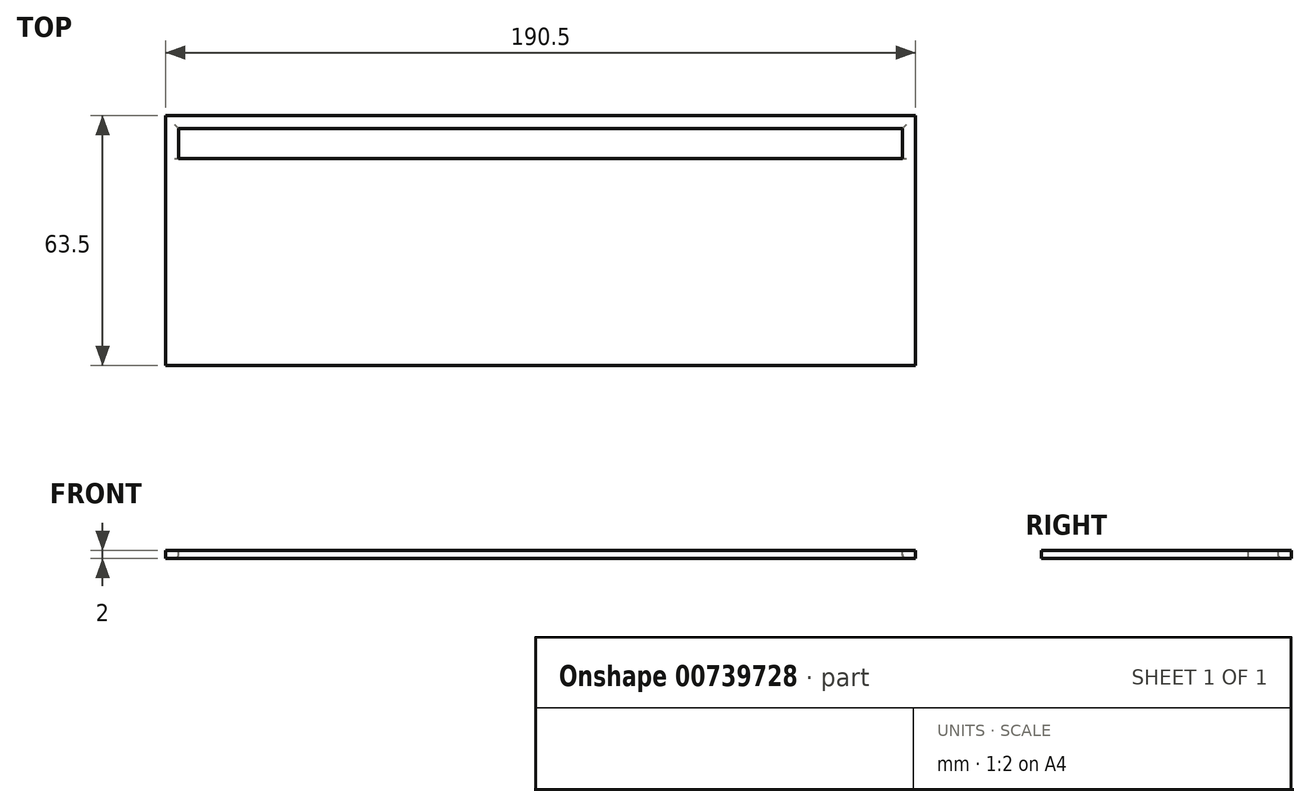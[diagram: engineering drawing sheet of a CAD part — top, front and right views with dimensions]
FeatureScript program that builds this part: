
annotation { "Feature Type Name" : "Feature", "Feature Type Description" : "" }
export const myFeature = defineFeature(function(context is Context, id is Id, definition is map)
    precondition{}
    {
        {
            var Q0;
            Q0=qCreatedBy(makeId("Top.planeOp"),FACE);
            var sketch = newSketch(context, id + "F0", { "sketchPlane" : qUnion([Q0])});
            skLineSegment(sketch, "E0.bottom", {"start": v(-93.46, 63.5) * mm, "end": v(97.04, 63.5) * mm});
            skLineSegment(sketch, "E0.top", {"start": v(-93.46, 0) * mm, "end": v(97.04, 0) * mm});
            skLineSegment(sketch, "E0.left", {"start": v(-93.46, 63.5) * mm, "end": v(-93.46, 0) * mm});
            skLineSegment(sketch, "E0.right", {"start": v(97.04, 63.5) * mm, "end": v(97.04, 0) * mm});
            skSolve(sketch);
        }
        {
            var Q0;
            Q0 = qSketchRegion(id + "F0", true);
            extrude(context, id + "F1", {"entities" : qUnion([Q0]), "depth" : 2 * mm, "offsetDistance" : 25.4 * mm});
        }
        {
            var Q0;
            Q0=makeQuery(id+"F1.opExtrude","CAP_FACE",FACE,{"disambiguationData":[OSD([sQuery(id+"F0.wireOp",EDGE,"E0.bottom"),sQuery(id+"F0.wireOp",EDGE,"E0.top"),sQuery(id+"F0.wireOp",EDGE,"E0.left"),sQuery(id+"F0.wireOp",EDGE,"E0.right")])],"isStart":false});
            var sketch = newSketch(context, id + "F2", { "sketchPlane" : qUnion([Q0])});
            skLineSegment(sketch, "E1.bottom", {"start": v(-90.16, 60.2) * mm, "end": v(93.74, 60.2) * mm});
            skLineSegment(sketch, "E1.top", {"start": v(-90.16, 52.58) * mm, "end": v(93.74, 52.58) * mm});
            skLineSegment(sketch, "E1.left", {"start": v(-90.16, 60.2) * mm, "end": v(-90.16, 52.58) * mm});
            skLineSegment(sketch, "E1.right", {"start": v(93.74, 60.2) * mm, "end": v(93.74, 52.58) * mm});
            skSolve(sketch);
        }
        {
            var Q0;
            Q0 = qSketchRegion(id + "F2", true);
            extrude(context, id + "F3", {"entities" : qUnion([Q0]), "operationType" : NewBodyOperationType.REMOVE, "oppositeDirection" : true, "depth" : 25.4 * mm, "offsetDistance" : 25.4 * mm});
        }
        {
            var Q0;
            Q0=makeQuery(id+"F3.boolean.opBoolean","COPY",EDGE,{"derivedFrom":makeQuery(id+"F3.opExtrude","CAP_EDGE",EDGE,{"disambiguationData":[OSD([sQuery(id+"F2.wireOp",EDGE,"E1.bottom")])],"isStart":true})});
            var Q1;
            Q1=makeQuery(id+"F3.boolean.opBoolean","INTERSECT",EDGE,{"derivedFrom":[makeQuery(id+"F1.opExtrude","CAP_FACE",FACE,{"disambiguationData":[OSD([sQuery(id+"F0.wireOp",EDGE,"E0.bottom"),sQuery(id+"F0.wireOp",EDGE,"E0.top"),sQuery(id+"F0.wireOp",EDGE,"E0.left"),sQuery(id+"F0.wireOp",EDGE,"E0.right")])],"isStart":true}),makeQuery(id+"F3.opExtrude","SWEPT_FACE",FACE,{"disambiguationData":[OSD([sQuery(id+"F2.wireOp",EDGE,"E1.bottom")])]})]});
            fillet(context, id + "F4", {"entities" : qUnion([Q0, Q1]), "radius" : 1 * mm, "tangentPropagation" : true, "allowEdgeOverflow" : false});
        }
        {
            var Q0;
            Q0=makeQuery(id+"F3.boolean.opBoolean","INTERSECT",EDGE,{"derivedFrom":[makeQuery(id+"F1.opExtrude","CAP_FACE",FACE,{"disambiguationData":[OSD([sQuery(id+"F0.wireOp",EDGE,"E0.bottom"),sQuery(id+"F0.wireOp",EDGE,"E0.top"),sQuery(id+"F0.wireOp",EDGE,"E0.left"),sQuery(id+"F0.wireOp",EDGE,"E0.right")])],"isStart":true}),makeQuery(id+"F3.opExtrude","SWEPT_FACE",FACE,{"disambiguationData":[OSD([sQuery(id+"F2.wireOp",EDGE,"E1.right")])]})]});
            var Q1;
            Q1=makeQuery(id+"F3.boolean.opBoolean","COPY",EDGE,{"derivedFrom":makeQuery(id+"F3.opExtrude","CAP_EDGE",EDGE,{"disambiguationData":[OSD([sQuery(id+"F2.wireOp",EDGE,"E1.right")])],"isStart":true})});
            var Q2;
            Q2=makeQuery(id+"F3.boolean.opBoolean","COPY",EDGE,{"derivedFrom":makeQuery(id+"F3.opExtrude","CAP_EDGE",EDGE,{"disambiguationData":[OSD([sQuery(id+"F2.wireOp",EDGE,"E1.left")])],"isStart":true})});
            var Q3;
            Q3=makeQuery(id+"F3.boolean.opBoolean","INTERSECT",EDGE,{"derivedFrom":[makeQuery(id+"F1.opExtrude","CAP_FACE",FACE,{"disambiguationData":[OSD([sQuery(id+"F0.wireOp",EDGE,"E0.bottom"),sQuery(id+"F0.wireOp",EDGE,"E0.top"),sQuery(id+"F0.wireOp",EDGE,"E0.left"),sQuery(id+"F0.wireOp",EDGE,"E0.right")])],"isStart":true}),makeQuery(id+"F3.opExtrude","SWEPT_FACE",FACE,{"disambiguationData":[OSD([sQuery(id+"F2.wireOp",EDGE,"E1.left")])]})]});
            fillet(context, id + "F5", {"entities" : qUnion([Q0, Q1, Q2, Q3]), "radius" : 1 * mm, "tangentPropagation" : true, "allowEdgeOverflow" : false});
        }
    });
